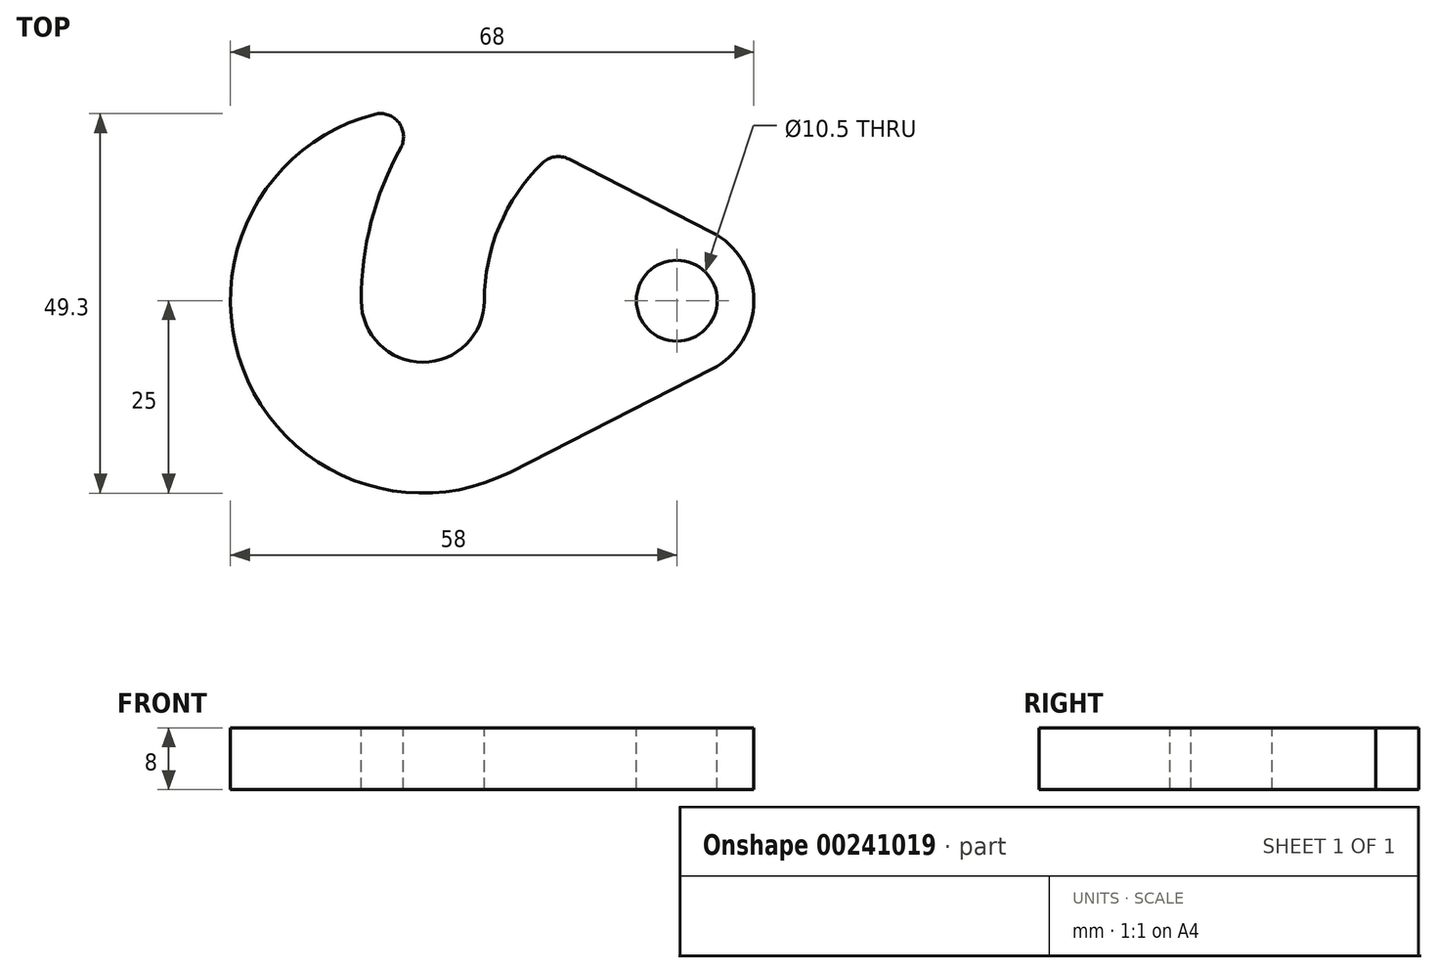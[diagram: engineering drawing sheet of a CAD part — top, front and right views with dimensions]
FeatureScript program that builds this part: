
annotation { "Feature Type Name" : "Feature", "Feature Type Description" : "" }
export const myFeature = defineFeature(function(context is Context, id is Id, definition is map)
    precondition{}
    {
        {
            var Q0;
            Q0=qCreatedBy(makeId("Top.planeOp"),FACE);
            var sketch = newSketch(context, id + "F0", { "sketchPlane" : qUnion([Q0])});
            skArc(sketch, "E0", {"start": v(-8, 0) * mm, "mid": v(0, -8) * mm, "end": v(8, 0) * mm});
            skArc(sketch, "E1", {"start": v(-6.25, 24.2) * mm, "mid": v(-23.38, -8.86) * mm, "end": v(11.36, -22.27) * mm});
            skPoint(sketch, "E2", {"position": v(0, 25) * mm});
            skPoint(sketch, "E3", {"position": v(-25, 0) * mm});
            skPoint(sketch, "E4", {"position": v(0, -25) * mm});
            skPoint(sketch, "E5", {"position": v(43, 0) * mm});
            skArc(sketch, "E6", {"start": v(37.55, -8.9) * mm, "mid": v(43, 0) * mm, "end": v(37.55, 8.9) * mm});
            skCircle(sketch, "E7", {"center": v(33, 0) * mm, "radius": 5.25 * mm, "construction": true});
            skArc(sketch, "E8", {"start": v(0, 0) * mm, "mid": v(6.42, 19.56) * mm, "end": v(23.18, 31.5) * mm, "construction": true});
            skArc(sketch, "E9.0", {"start": v(8, 0) * mm, "mid": v(9.95, 9.69) * mm, "end": v(15.5, 17.86) * mm});
            skArc(sketch, "E10.0", {"start": v(-8, 0) * mm, "mid": v(-6.7, 10.25) * mm, "end": v(-2.88, 19.85) * mm});
            skLineSegment(sketch, "E11", {"start": v(11.36, -22.27) * mm, "end": v(37.55, -8.9) * mm});
            skArc(sketch, "E12", {"start": v(-2.88, 19.85) * mm, "mid": v(-3.13, 23.14) * mm, "end": v(-6.25, 24.2) * mm});
            skLineSegment(sketch, "E13", {"start": v(37.55, 8.9) * mm, "end": v(18.97, 18.39) * mm});
            skArc(sketch, "E14.filletArc", {"start": v(18.97, 18.39) * mm, "mid": v(17.15, 18.68) * mm, "end": v(15.5, 17.86) * mm});
            skSolve(sketch);
        }
        {
            var Q0;
            Q0 = qSketchRegion(id + "F0", true);
            extrude(context, id + "F1", {"entities" : qUnion([Q0]), "oppositeDirection" : true, "depth" : 8 * mm});
        }
        {
            var Q0;
            Q0=makeQuery(id+"F0.imprint","IMPRINT",FACE,{"disambiguationData":[TD([[makeQuery(id+"F0.imprint","IMPRINT",EDGE,{"derivedFrom":sQuery(id+"F0.wireOp",EDGE,"E0")}),-1.0]])]});
            var sketch = newSketch(context, id + "F2", { "sketchPlane" : qUnion([Q0])});
            skPoint(sketch, "E15", {"position": v(33, 0) * mm});
            skSolve(sketch);
        }
        {
            var Q0;
            Q0=sQuery(id+"F2.wireOp",VERTEX,"E15");
            var Q1;
            Q1=makeQuery(id+"F1.opExtrude","SWEPT_BODY",BODY,{"disambiguationData":[OSD([sQuery(id+"F0.wireOp",EDGE,"E0"),sQuery(id+"F0.wireOp",EDGE,"E1"),sQuery(id+"F0.wireOp",EDGE,"E6"),sQuery(id+"F0.wireOp",EDGE,"E9.0"),sQuery(id+"F0.wireOp",EDGE,"E10.0"),sQuery(id+"F0.wireOp",EDGE,"E11"),sQuery(id+"F0.wireOp",EDGE,"E12"),sQuery(id+"F0.wireOp",EDGE,"E13"),sQuery(id+"F0.wireOp",EDGE,"E14.filletArc")])]});
            hole(context, id + "F3", {"style" : HoleStyle.SIMPLE, "endStyle" : HoleEndStyle.THROUGH, "holeDiameter" : 10.5 * mm, "locations" : qUnion([Q0]), "scope" : qUnion([Q1]), "isTappedThrough" : true});
        }
    });
